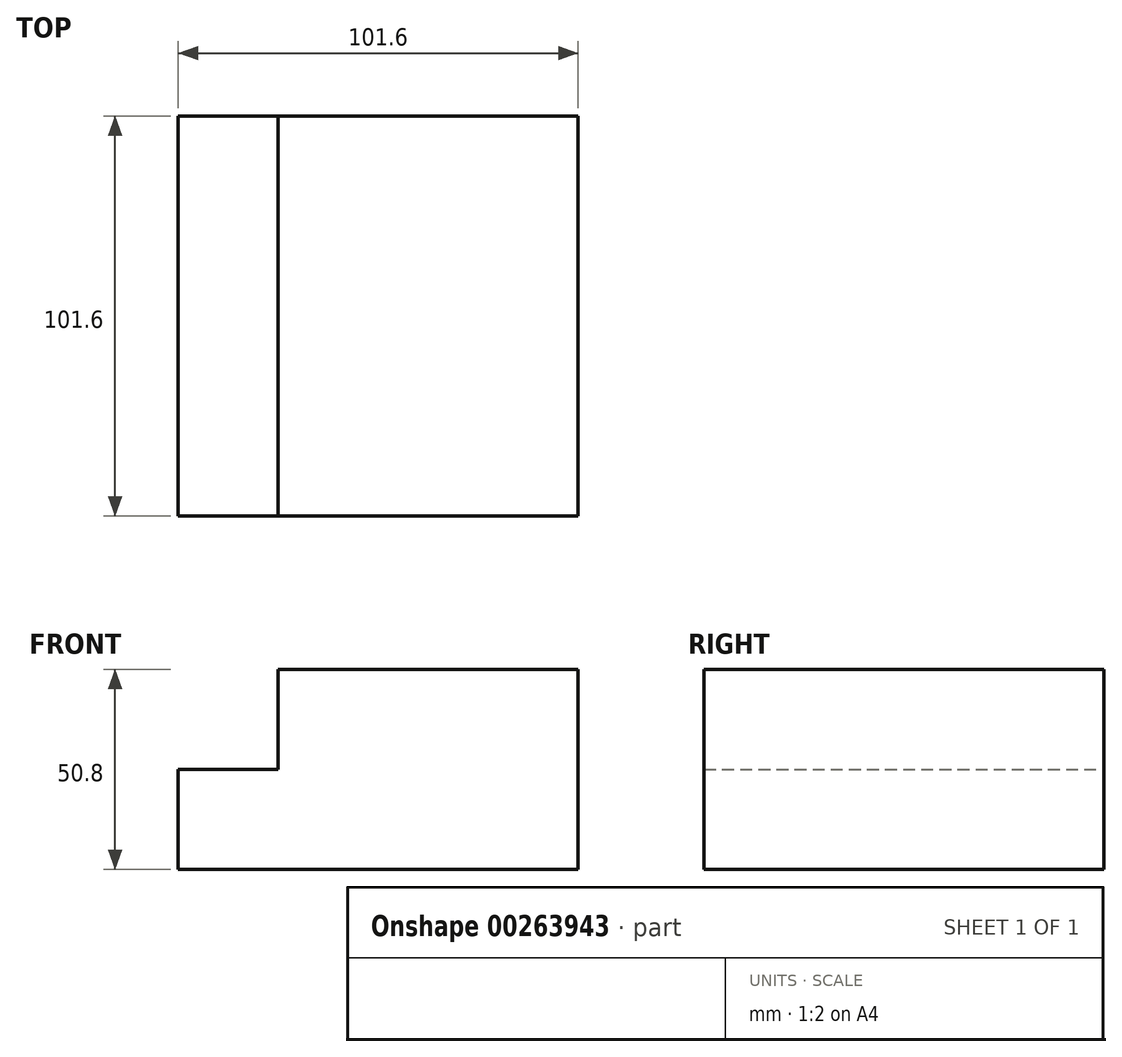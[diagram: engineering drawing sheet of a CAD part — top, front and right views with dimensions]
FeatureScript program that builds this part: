
annotation { "Feature Type Name" : "Feature", "Feature Type Description" : "" }
export const myFeature = defineFeature(function(context is Context, id is Id, definition is map)
    precondition{}
    {
        {
            var Q0;
            Q0=qCreatedBy(makeId("Front.planeOp"),FACE);
            var sketch = newSketch(context, id + "F0", { "sketchPlane" : qUnion([Q0])});
            skLineSegment(sketch, "E0", {"start": v(-76.12, 0) * mm, "end": v(-76.12, 25.4) * mm});
            skLineSegment(sketch, "E1", {"start": v(-76.12, 25.4) * mm, "end": v(-50.72, 25.4) * mm});
            skLineSegment(sketch, "E2", {"start": v(-50.72, 25.4) * mm, "end": v(-50.72, 50.8) * mm});
            skLineSegment(sketch, "E3", {"start": v(-50.72, 50.8) * mm, "end": v(25.48, 50.8) * mm});
            skLineSegment(sketch, "E4", {"start": v(25.48, 50.8) * mm, "end": v(25.48, 0) * mm});
            skLineSegment(sketch, "E5", {"start": v(25.48, 0) * mm, "end": v(-76.12, 0) * mm});
            skSolve(sketch);
        }
        {
            var Q0;
            Q0 = qSketchRegion(id + "F0", true);
            extrude(context, id + "F1", {"entities" : qUnion([Q0]), "depth" : 101.6 * mm});
        }
    });
